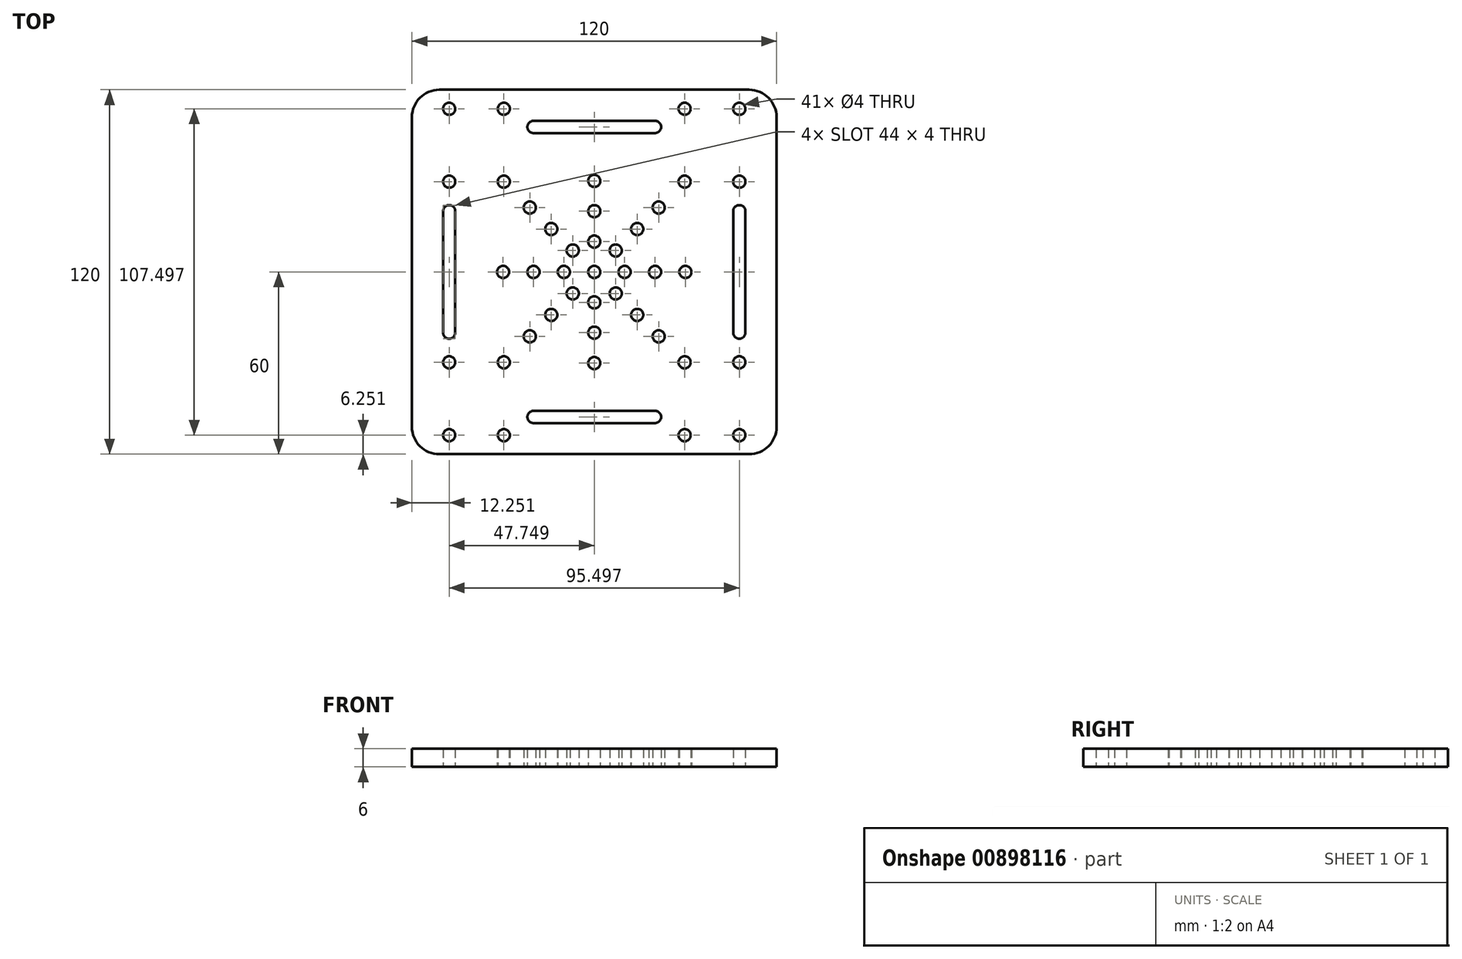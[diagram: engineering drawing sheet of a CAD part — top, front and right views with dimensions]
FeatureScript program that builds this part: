
annotation { "Feature Type Name" : "Feature", "Feature Type Description" : "" }
export const myFeature = defineFeature(function(context is Context, id is Id, definition is map)
    precondition{}
    {
        {
            var Q0;
            Q0=qCreatedBy(makeId("Front.planeOp"),FACE);
            var sketch = newSketch(context, id + "F0", { "sketchPlane" : qUnion([Q0])});
            skLineSegment(sketch, "E0.bottom", {"start": v(0, 0) * mm, "end": v(120, 0) * mm});
            skLineSegment(sketch, "E0.top", {"start": v(0, 6) * mm, "end": v(120, 6) * mm});
            skLineSegment(sketch, "E0.left", {"start": v(0, 0) * mm, "end": v(0, 6) * mm});
            skLineSegment(sketch, "E0.right", {"start": v(120, 0) * mm, "end": v(120, 6) * mm});
            skSolve(sketch);
        }
        {
            var Q0;
            Q0=makeQuery(id+"F0.imprint","IMPRINT",FACE,{"disambiguationData":[TD([[makeQuery(id+"F0.imprint","IMPRINT",EDGE,{"derivedFrom":sQuery(id+"F0.wireOp",EDGE,"E0.bottom")}),1.0]])]});
            extrude(context, id + "F1", {"entities" : qUnion([Q0]), "depth" : 120 * mm, "offsetDistance" : 25 * mm});
        }
        {
            var Q0;
            Q0=qCreatedBy(makeId("Top.planeOp"),FACE);
            var sketch = newSketch(context, id + "F2", { "sketchPlane" : qUnion([Q0])});
            skLineSegment(sketch, "E1", {"start": v(0, -9) * mm, "end": v(0, -111) * mm});
            skLineSegment(sketch, "E2", {"start": v(9, -120) * mm, "end": v(111, -120) * mm});
            skLineSegment(sketch, "E3", {"start": v(120, -111) * mm, "end": v(120, -9) * mm});
            skLineSegment(sketch, "E4", {"start": v(111, 0) * mm, "end": v(9, 0) * mm});
            skLineSegment(sketch, "E5", {"start": v(0, 0) * mm, "end": v(120, -120) * mm});
            skLineSegment(sketch, "E6", {"start": v(120, 0) * mm, "end": v(0, -120) * mm});
            skPoint(sketch, "E7", {"position": v(60, -60) * mm});
            skCircle(sketch, "E8", {"center": v(60, -60) * mm, "radius": 35 * mm});
            skLineSegment(sketch, "E9.bottom", {"start": v(0, 0) * mm, "end": v(35.25, 0) * mm});
            skLineSegment(sketch, "E9.top", {"start": v(0, -35.25) * mm, "end": v(35.25, -35.25) * mm});
            skLineSegment(sketch, "E9.left", {"start": v(0, 0) * mm, "end": v(0, -35.25) * mm});
            skLineSegment(sketch, "E9.right", {"start": v(35.25, 0) * mm, "end": v(35.25, -35.25) * mm});
            skLineSegment(sketch, "E10.bottom", {"start": v(84.75, -35.25) * mm, "end": v(120, -35.25) * mm});
            skLineSegment(sketch, "E10.top", {"start": v(84.75, 0) * mm, "end": v(120, 0) * mm});
            skLineSegment(sketch, "E10.left", {"start": v(84.75, -35.25) * mm, "end": v(84.75, 0) * mm});
            skLineSegment(sketch, "E10.right", {"start": v(120, -35.25) * mm, "end": v(120, 0) * mm});
            skLineSegment(sketch, "E11.bottom", {"start": v(0, -120) * mm, "end": v(35.25, -120) * mm});
            skLineSegment(sketch, "E11.top", {"start": v(0, -84.75) * mm, "end": v(35.25, -84.75) * mm});
            skLineSegment(sketch, "E11.left", {"start": v(0, -120) * mm, "end": v(0, -84.75) * mm});
            skLineSegment(sketch, "E11.right", {"start": v(35.25, -120) * mm, "end": v(35.25, -84.75) * mm});
            skLineSegment(sketch, "E12.bottom", {"start": v(120, -120) * mm, "end": v(84.75, -120) * mm});
            skLineSegment(sketch, "E12.top", {"start": v(120, -84.75) * mm, "end": v(84.75, -84.75) * mm});
            skLineSegment(sketch, "E12.left", {"start": v(120, -120) * mm, "end": v(120, -84.75) * mm});
            skLineSegment(sketch, "E12.right", {"start": v(84.75, -120) * mm, "end": v(84.75, -84.75) * mm});
            skPoint(sketch, "E13", {"position": v(30.25, -89.75) * mm});
            skCircle(sketch, "E14", {"center": v(30.25, -89.75) * mm, "radius": 2 * mm});
            skPoint(sketch, "E15.0.1.0", {"position": v(30.25, -113.75) * mm});
            skCircle(sketch, "E15.0.1.1", {"center": v(30.25, -113.75) * mm, "radius": 2 * mm});
            skPoint(sketch, "E15.1.0.0", {"position": v(12.25, -89.75) * mm});
            skCircle(sketch, "E15.1.0.1", {"center": v(12.25, -89.75) * mm, "radius": 2 * mm});
            skPoint(sketch, "E15.1.1.0", {"position": v(12.25, -113.75) * mm});
            skCircle(sketch, "E15.1.1.1", {"center": v(12.25, -113.75) * mm, "radius": 2 * mm});
            skLineSegment(sketch, "E15.direction1", {"start": v(30.25, -89.75) * mm, "end": v(12.25, -89.75) * mm, "construction": true});
            skLineSegment(sketch, "E15.direction2", {"start": v(30.25, -89.75) * mm, "end": v(30.25, -113.75) * mm, "construction": true});
            skPoint(sketch, "E16", {"position": v(89.75, -30.25) * mm});
            skCircle(sketch, "E17", {"center": v(89.75, -30.25) * mm, "radius": 2 * mm});
            skCircle(sketch, "E18.0.1.0", {"center": v(89.75, -6.25) * mm, "radius": 2 * mm});
            skCircle(sketch, "E18.1.0.0", {"center": v(107.75, -30.25) * mm, "radius": 2 * mm});
            skCircle(sketch, "E18.1.1.0", {"center": v(107.75, -6.25) * mm, "radius": 2 * mm});
            skLineSegment(sketch, "E18.direction1", {"start": v(89.75, -30.25) * mm, "end": v(107.75, -30.25) * mm, "construction": true});
            skLineSegment(sketch, "E18.direction2", {"start": v(89.75, -30.25) * mm, "end": v(89.75, -6.25) * mm, "construction": true});
            skPoint(sketch, "E19", {"position": v(30.25, -30.25) * mm});
            skCircle(sketch, "E20", {"center": v(30.25, -30.25) * mm, "radius": 2 * mm});
            skPoint(sketch, "E21.0.1.0", {"position": v(30.25, -6.25) * mm});
            skCircle(sketch, "E21.0.1.1", {"center": v(30.25, -6.25) * mm, "radius": 2 * mm});
            skPoint(sketch, "E21.1.0.0", {"position": v(12.25, -30.25) * mm});
            skCircle(sketch, "E21.1.0.1", {"center": v(12.25, -30.25) * mm, "radius": 2 * mm});
            skPoint(sketch, "E21.1.1.0", {"position": v(12.25, -6.25) * mm});
            skCircle(sketch, "E21.1.1.1", {"center": v(12.25, -6.25) * mm, "radius": 2 * mm});
            skLineSegment(sketch, "E21.direction1", {"start": v(30.25, -30.25) * mm, "end": v(12.25, -30.25) * mm, "construction": true});
            skLineSegment(sketch, "E21.direction2", {"start": v(30.25, -30.25) * mm, "end": v(30.25, -6.25) * mm, "construction": true});
            skPoint(sketch, "E22", {"position": v(89.75, -89.75) * mm});
            skCircle(sketch, "E23", {"center": v(89.75, -89.75) * mm, "radius": 2 * mm});
            skPoint(sketch, "E24.0.1.0", {"position": v(89.75, -113.75) * mm});
            skCircle(sketch, "E24.0.1.1", {"center": v(89.75, -113.75) * mm, "radius": 2 * mm});
            skPoint(sketch, "E24.1.0.0", {"position": v(107.75, -89.75) * mm});
            skCircle(sketch, "E24.1.0.1", {"center": v(107.75, -89.75) * mm, "radius": 2 * mm});
            skPoint(sketch, "E24.1.1.0", {"position": v(107.75, -113.75) * mm});
            skCircle(sketch, "E24.1.1.1", {"center": v(107.75, -113.75) * mm, "radius": 2 * mm});
            skLineSegment(sketch, "E24.direction1", {"start": v(89.75, -89.75) * mm, "end": v(107.75, -89.75) * mm, "construction": true});
            skLineSegment(sketch, "E24.direction2", {"start": v(89.75, -89.75) * mm, "end": v(89.75, -113.75) * mm, "construction": true});
            skCircle(sketch, "E25", {"center": v(60, -60) * mm, "radius": 2 * mm});
            skLineSegment(sketch, "E26", {"start": v(0, -60) * mm, "end": v(120, -60) * mm});
            skLineSegment(sketch, "E27", {"start": v(60, 0) * mm, "end": v(60, -120) * mm});
            skCircle(sketch, "E28", {"center": v(60, -60) * mm, "radius": 10 * mm});
            skCircle(sketch, "E29", {"center": v(67.07, -52.93) * mm, "radius": 2 * mm});
            skCircle(sketch, "E30", {"center": v(60, -50) * mm, "radius": 2 * mm});
            skCircle(sketch, "E31", {"center": v(52.93, -52.93) * mm, "radius": 2 * mm});
            skCircle(sketch, "E32", {"center": v(50, -60) * mm, "radius": 2 * mm});
            skCircle(sketch, "E33", {"center": v(52.93, -67.07) * mm, "radius": 2 * mm});
            skCircle(sketch, "E34", {"center": v(60, -70) * mm, "radius": 2 * mm});
            skCircle(sketch, "E35", {"center": v(67.07, -67.07) * mm, "radius": 2 * mm});
            skCircle(sketch, "E36", {"center": v(70, -60) * mm, "radius": 2 * mm});
            skCircle(sketch, "E37", {"center": v(60, -60) * mm, "radius": 20 * mm});
            skCircle(sketch, "E38", {"center": v(80, -60) * mm, "radius": 2 * mm});
            skCircle(sketch, "E39", {"center": v(74.14, -45.86) * mm, "radius": 2 * mm});
            skCircle(sketch, "E40", {"center": v(60, -40) * mm, "radius": 2 * mm});
            skCircle(sketch, "E41", {"center": v(40, -60) * mm, "radius": 2 * mm});
            skCircle(sketch, "E42", {"center": v(45.86, -74.14) * mm, "radius": 2 * mm});
            skCircle(sketch, "E43", {"center": v(60, -80) * mm, "radius": 2 * mm});
            skCircle(sketch, "E44", {"center": v(74.14, -74.14) * mm, "radius": 2 * mm});
            skCircle(sketch, "E45", {"center": v(60, -60) * mm, "radius": 30 * mm});
            skCircle(sketch, "E46", {"center": v(90, -60) * mm, "radius": 2 * mm});
            skCircle(sketch, "E47", {"center": v(81.21, -38.79) * mm, "radius": 2 * mm});
            skCircle(sketch, "E48", {"center": v(81.21, -81.21) * mm, "radius": 2 * mm});
            skCircle(sketch, "E49", {"center": v(60, -30) * mm, "radius": 2 * mm});
            skCircle(sketch, "E50", {"center": v(38.79, -38.79) * mm, "radius": 2 * mm});
            skCircle(sketch, "E51", {"center": v(30, -60) * mm, "radius": 2 * mm});
            skCircle(sketch, "E52", {"center": v(38.79, -81.21) * mm, "radius": 2 * mm});
            skCircle(sketch, "E53", {"center": v(60, -90) * mm, "radius": 2 * mm});
            skCircle(sketch, "E54", {"center": v(45.86, -45.86) * mm, "radius": 2 * mm});
            skLineSegment(sketch, "E55.left", {"start": v(14.25, -40) * mm, "end": v(14.25, -80) * mm});
            skLineSegment(sketch, "E55.right", {"start": v(10.25, -40) * mm, "end": v(10.25, -80) * mm});
            skPoint(sketch, "E55.middle", {"position": v(12.25, -60) * mm});
            skArc(sketch, "E56", {"start": v(14.25, -40) * mm, "mid": v(12.25, -38) * mm, "end": v(10.25, -40) * mm});
            skArc(sketch, "E57", {"start": v(10.25, -80) * mm, "mid": v(12.25, -82) * mm, "end": v(14.25, -80) * mm});
            skPoint(sketch, "E58.1.0", {"position": v(60, -107.75) * mm});
            skArc(sketch, "E58.1.1", {"start": v(40, -105.75) * mm, "mid": v(38, -107.75) * mm, "end": v(40, -109.75) * mm});
            skArc(sketch, "E58.1.2", {"start": v(80, -109.75) * mm, "mid": v(82, -107.75) * mm, "end": v(80, -105.75) * mm});
            skLineSegment(sketch, "E58.1.3", {"start": v(40, -105.75) * mm, "end": v(80, -105.75) * mm});
            skLineSegment(sketch, "E58.1.4", {"start": v(40, -109.75) * mm, "end": v(80, -109.75) * mm});
            skPoint(sketch, "E58.2.0", {"position": v(107.75, -60) * mm});
            skArc(sketch, "E58.2.1", {"start": v(105.75, -80) * mm, "mid": v(107.75, -82) * mm, "end": v(109.75, -80) * mm});
            skArc(sketch, "E58.2.2", {"start": v(109.75, -40) * mm, "mid": v(107.75, -38) * mm, "end": v(105.75, -40) * mm});
            skLineSegment(sketch, "E58.2.3", {"start": v(105.75, -80) * mm, "end": v(105.75, -40) * mm});
            skLineSegment(sketch, "E58.2.4", {"start": v(109.75, -80) * mm, "end": v(109.75, -40) * mm});
            skPoint(sketch, "E58.3.0", {"position": v(60, -12.25) * mm});
            skArc(sketch, "E58.3.1", {"start": v(80, -14.25) * mm, "mid": v(82, -12.25) * mm, "end": v(80, -10.25) * mm});
            skArc(sketch, "E58.3.2", {"start": v(40, -10.25) * mm, "mid": v(38, -12.25) * mm, "end": v(40, -14.25) * mm});
            skLineSegment(sketch, "E58.3.3", {"start": v(80, -14.25) * mm, "end": v(40, -14.25) * mm});
            skLineSegment(sketch, "E58.3.4", {"start": v(80, -10.25) * mm, "end": v(40, -10.25) * mm});
            skPoint(sketch, "E59.visualSharp", {"position": v(0, -120) * mm});
            skArc(sketch, "E59.filletArc", {"start": v(0, -111) * mm, "mid": v(2.64, -117.36) * mm, "end": v(9, -120) * mm});
            skPoint(sketch, "E60.visualSharp", {"position": v(0, 0) * mm});
            skArc(sketch, "E60.filletArc", {"start": v(9, 0) * mm, "mid": v(2.64, -2.64) * mm, "end": v(0, -9) * mm});
            skPoint(sketch, "E61.visualSharp", {"position": v(120, 0) * mm});
            skArc(sketch, "E61.filletArc", {"start": v(120, -9) * mm, "mid": v(117.36, -2.64) * mm, "end": v(111, 0) * mm});
            skPoint(sketch, "E62.visualSharp", {"position": v(120, -120) * mm});
            skArc(sketch, "E62.filletArc", {"start": v(111, -120) * mm, "mid": v(117.36, -117.36) * mm, "end": v(120, -111) * mm});
            skSolve(sketch);
        }
        {
            var Q0;
            Q0=sQuery(id+"F2.wireOp",VERTEX,"E15.1.1.0");
            var Q1;
            Q1=sQuery(id+"F2.wireOp",VERTEX,"E15.1.0.0");
            var Q2;
            Q2=sQuery(id+"F2.wireOp",VERTEX,"E13");
            var Q3;
            Q3=sQuery(id+"F2.wireOp",VERTEX,"E15.0.1.0");
            var Q4;
            Q4=sQuery(id+"F2.wireOp",VERTEX,"E24.0.1.0");
            var Q5;
            Q5=sQuery(id+"F2.wireOp",VERTEX,"E22");
            var Q6;
            Q6=sQuery(id+"F2.wireOp",VERTEX,"E24.1.0.0");
            var Q7;
            Q7=sQuery(id+"F2.wireOp",VERTEX,"E24.1.1.0");
            var Q8;
            Q8=sQuery(id+"F2.wireOp",VERTEX,"E18.direction1.end");
            var Q9;
            Q9=sQuery(id+"F2.wireOp",VERTEX,"E16");
            var Q10;
            Q10=sQuery(id+"F2.wireOp",VERTEX,"E18.direction2.end");
            var Q11;
            Q11=sQuery(id+"F2.wireOp",VERTEX,"E18.1.1.0.center");
            var Q12;
            Q12=sQuery(id+"F2.wireOp",VERTEX,"E21.0.1.0");
            var Q13;
            Q13=sQuery(id+"F2.wireOp",VERTEX,"E21.1.0.0");
            var Q14;
            Q14=sQuery(id+"F2.wireOp",VERTEX,"E19");
            var Q15;
            Q15=sQuery(id+"F2.wireOp",VERTEX,"E21.1.1.0");
            var Q16;
            Q16=sQuery(id+"F2.wireOp",VERTEX,"E50.center");
            var Q17;
            Q17=sQuery(id+"F2.wireOp",VERTEX,"E54.center");
            var Q18;
            Q18=sQuery(id+"F2.wireOp",VERTEX,"E51.center");
            var Q19;
            Q19=sQuery(id+"F2.wireOp",VERTEX,"E41.center");
            var Q20;
            Q20=sQuery(id+"F2.wireOp",VERTEX,"E42.center");
            var Q21;
            Q21=sQuery(id+"F2.wireOp",VERTEX,"E52.center");
            var Q22;
            Q22=sQuery(id+"F2.wireOp",VERTEX,"E43.center");
            var Q23;
            Q23=sQuery(id+"F2.wireOp",VERTEX,"E53.center");
            var Q24;
            Q24=sQuery(id+"F2.wireOp",VERTEX,"E48.center");
            var Q25;
            Q25=sQuery(id+"F2.wireOp",VERTEX,"E44.center");
            var Q26;
            Q26=sQuery(id+"F2.wireOp",VERTEX,"E38.center");
            var Q27;
            Q27=sQuery(id+"F2.wireOp",VERTEX,"E46.center");
            var Q28;
            Q28=sQuery(id+"F2.wireOp",VERTEX,"E47.center");
            var Q29;
            Q29=sQuery(id+"F2.wireOp",VERTEX,"E39.center");
            var Q30;
            Q30=sQuery(id+"F2.wireOp",VERTEX,"E40.center");
            var Q31;
            Q31=sQuery(id+"F2.wireOp",VERTEX,"E49.center");
            var Q32;
            Q32=sQuery(id+"F2.wireOp",VERTEX,"E33.center");
            var Q33;
            Q33=sQuery(id+"F2.wireOp",VERTEX,"E7");
            var Q34;
            Q34=sQuery(id+"F2.wireOp",VERTEX,"E32.center");
            var Q35;
            Q35=sQuery(id+"F2.wireOp",VERTEX,"E31.center");
            var Q36;
            Q36=sQuery(id+"F2.wireOp",VERTEX,"E30.center");
            var Q37;
            Q37=sQuery(id+"F2.wireOp",VERTEX,"E29.center");
            var Q38;
            Q38=sQuery(id+"F2.wireOp",VERTEX,"E36.center");
            var Q39;
            Q39=sQuery(id+"F2.wireOp",VERTEX,"E35.center");
            var Q40;
            Q40=sQuery(id+"F2.wireOp",VERTEX,"E34.center");
            var Q41;
            Q41=makeQuery(id+"F1.opExtrude","SWEPT_BODY",BODY,{"disambiguationData":[OSD([sQuery(id+"F0.wireOp",EDGE,"E0.bottom"),sQuery(id+"F0.wireOp",EDGE,"E0.top"),sQuery(id+"F0.wireOp",EDGE,"E0.left"),sQuery(id+"F0.wireOp",EDGE,"E0.right")])]});
            hole(context, id + "F3", {"style" : HoleStyle.SIMPLE, "endStyle" : HoleEndStyle.BLIND, "oppositeDirection" : true, "holeDiameter" : 4 * mm, "majorDiameter" : 5 * mm, "holeDepth" : 8 * mm, "isTappedThrough" : true, "tappedDepth" : 12 * mm, "tapClearance" : 3, "locations" : qUnion([Q0, Q1, Q2, Q3, Q4, Q5, Q6, Q7, Q8, Q9, Q10, Q11, Q12, Q13, Q14, Q15, Q16, Q17, Q18, Q19, Q20, Q21, Q22, Q23, Q24, Q25, Q26, Q27, Q28, Q29, Q30, Q31, Q32, Q33, Q34, Q35, Q36, Q37, Q38, Q39, Q40]), "scope" : qUnion([Q41])});
        }
        {
            var Q0;
            {var subQ5=sQuery(id+"F2.wireOp",EDGE,"E56");Q0=makeQuery(id+"F2.imprint","IMPRINT",FACE,{"disambiguationData":[TD([[makeQuery(id+"F2.imprint","IMPRINT",EDGE,{"derivedFrom":subQ5}),1.0]])]});}
            var Q1;
            {var subQ5=sQuery(id+"F2.wireOp",EDGE,"E57");Q1=makeQuery(id+"F2.imprint","IMPRINT",FACE,{"disambiguationData":[TD([[makeQuery(id+"F2.imprint","IMPRINT",EDGE,{"derivedFrom":subQ5}),1.0]])]});}
            var Q2;
            {var subQ5=sQuery(id+"F2.wireOp",EDGE,"E58.1.1");Q2=makeQuery(id+"F2.imprint","IMPRINT",FACE,{"disambiguationData":[TD([[makeQuery(id+"F2.imprint","IMPRINT",EDGE,{"derivedFrom":subQ5}),1.0]])]});}
            var Q3;
            {var subQ5=sQuery(id+"F2.wireOp",EDGE,"E58.1.2");Q3=makeQuery(id+"F2.imprint","IMPRINT",FACE,{"disambiguationData":[TD([[makeQuery(id+"F2.imprint","IMPRINT",EDGE,{"derivedFrom":subQ5}),1.0]])]});}
            var Q4;
            {var subQ5=sQuery(id+"F2.wireOp",EDGE,"E58.2.2");Q4=makeQuery(id+"F2.imprint","IMPRINT",FACE,{"disambiguationData":[TD([[makeQuery(id+"F2.imprint","IMPRINT",EDGE,{"derivedFrom":subQ5}),1.0]])]});}
            var Q5;
            {var subQ5=sQuery(id+"F2.wireOp",EDGE,"E58.2.1");Q5=makeQuery(id+"F2.imprint","IMPRINT",FACE,{"disambiguationData":[TD([[makeQuery(id+"F2.imprint","IMPRINT",EDGE,{"derivedFrom":subQ5}),1.0]])]});}
            var Q6;
            {var subQ5=sQuery(id+"F2.wireOp",EDGE,"E58.3.2");Q6=makeQuery(id+"F2.imprint","IMPRINT",FACE,{"disambiguationData":[TD([[makeQuery(id+"F2.imprint","IMPRINT",EDGE,{"derivedFrom":subQ5}),1.0]])]});}
            var Q7;
            {var subQ5=sQuery(id+"F2.wireOp",EDGE,"E58.3.1");Q7=makeQuery(id+"F2.imprint","IMPRINT",FACE,{"disambiguationData":[TD([[makeQuery(id+"F2.imprint","IMPRINT",EDGE,{"derivedFrom":subQ5}),1.0]])]});}
            extrude(context, id + "F4", {"entities" : qUnion([Q0, Q1, Q2, Q3, Q4, Q5, Q6, Q7]), "operationType" : NewBodyOperationType.REMOVE, "depth" : 8 * mm, "offsetDistance" : 25 * mm});
        }
        {
            var Q0;
            {var subQ0=sQuery(id+"F2.wireOp",EDGE,"E12.left");var subQ3=sQuery(id+"F2.wireOp",EDGE,"E62.filletArc");var subQ5=makeQuery(id+"F2.imprint","INTERSECT",VERTEX,{"derivedFrom":[subQ0,subQ3]});Q0=makeQuery(id+"F2.imprint","IMPRINT",FACE,{"disambiguationData":[TD([[makeQuery(id+"F2.imprint","IMPRINT",EDGE,{"disambiguationData":[TD([[subQ5,1.0]])],"derivedFrom":subQ3}),-1.0]])]});}
            var Q1;
            {var subQ0=sQuery(id+"F2.wireOp",EDGE,"E12.bottom");var subQ3=sQuery(id+"F2.wireOp",EDGE,"E62.filletArc");var subQ5=makeQuery(id+"F2.imprint","INTERSECT",VERTEX,{"derivedFrom":[subQ0,subQ3]});Q1=makeQuery(id+"F2.imprint","IMPRINT",FACE,{"disambiguationData":[TD([[makeQuery(id+"F2.imprint","IMPRINT",EDGE,{"disambiguationData":[TD([[subQ5,-1.0]])],"derivedFrom":subQ3}),-1.0]])]});}
            var Q2;
            {var subQ0=sQuery(id+"F2.wireOp",EDGE,"E11.bottom");var subQ3=sQuery(id+"F2.wireOp",EDGE,"E59.filletArc");var subQ5=makeQuery(id+"F2.imprint","INTERSECT",VERTEX,{"derivedFrom":[subQ0,subQ3]});Q2=makeQuery(id+"F2.imprint","IMPRINT",FACE,{"disambiguationData":[TD([[makeQuery(id+"F2.imprint","IMPRINT",EDGE,{"disambiguationData":[TD([[subQ5,1.0]])],"derivedFrom":subQ3}),-1.0]])]});}
            var Q3;
            {var subQ0=sQuery(id+"F2.wireOp",EDGE,"E11.left");var subQ3=sQuery(id+"F2.wireOp",EDGE,"E59.filletArc");var subQ5=makeQuery(id+"F2.imprint","INTERSECT",VERTEX,{"derivedFrom":[subQ0,subQ3]});Q3=makeQuery(id+"F2.imprint","IMPRINT",FACE,{"disambiguationData":[TD([[makeQuery(id+"F2.imprint","IMPRINT",EDGE,{"disambiguationData":[TD([[subQ5,-1.0]])],"derivedFrom":subQ3}),-1.0]])]});}
            var Q4;
            {var subQ0=sQuery(id+"F2.wireOp",EDGE,"E10.right");var subQ3=sQuery(id+"F2.wireOp",EDGE,"E61.filletArc");var subQ5=makeQuery(id+"F2.imprint","INTERSECT",VERTEX,{"derivedFrom":[subQ0,subQ3]});Q4=makeQuery(id+"F2.imprint","IMPRINT",FACE,{"disambiguationData":[TD([[makeQuery(id+"F2.imprint","IMPRINT",EDGE,{"disambiguationData":[TD([[subQ5,-1.0]])],"derivedFrom":subQ3}),-1.0]])]});}
            var Q5;
            {var subQ0=sQuery(id+"F2.wireOp",EDGE,"E10.top");var subQ3=sQuery(id+"F2.wireOp",EDGE,"E61.filletArc");var subQ5=makeQuery(id+"F2.imprint","INTERSECT",VERTEX,{"derivedFrom":[subQ0,subQ3]});Q5=makeQuery(id+"F2.imprint","IMPRINT",FACE,{"disambiguationData":[TD([[makeQuery(id+"F2.imprint","IMPRINT",EDGE,{"disambiguationData":[TD([[subQ5,1.0]])],"derivedFrom":subQ3}),-1.0]])]});}
            var Q6;
            {var subQ0=sQuery(id+"F2.wireOp",EDGE,"E9.left");var subQ3=sQuery(id+"F2.wireOp",EDGE,"E60.filletArc");var subQ5=makeQuery(id+"F2.imprint","INTERSECT",VERTEX,{"derivedFrom":[subQ0,subQ3]});Q6=makeQuery(id+"F2.imprint","IMPRINT",FACE,{"disambiguationData":[TD([[makeQuery(id+"F2.imprint","IMPRINT",EDGE,{"disambiguationData":[TD([[subQ5,1.0]])],"derivedFrom":subQ3}),-1.0]])]});}
            var Q7;
            {var subQ0=sQuery(id+"F2.wireOp",EDGE,"E9.bottom");var subQ3=sQuery(id+"F2.wireOp",EDGE,"E60.filletArc");var subQ5=makeQuery(id+"F2.imprint","INTERSECT",VERTEX,{"derivedFrom":[subQ0,subQ3]});Q7=makeQuery(id+"F2.imprint","IMPRINT",FACE,{"disambiguationData":[TD([[makeQuery(id+"F2.imprint","IMPRINT",EDGE,{"disambiguationData":[TD([[subQ5,-1.0]])],"derivedFrom":subQ3}),-1.0]])]});}
            extrude(context, id + "F5", {"entities" : qUnion([Q0, Q1, Q2, Q3, Q4, Q5, Q6, Q7]), "operationType" : NewBodyOperationType.REMOVE, "depth" : 6 * mm, "offsetDistance" : 25 * mm});
        }
    });
